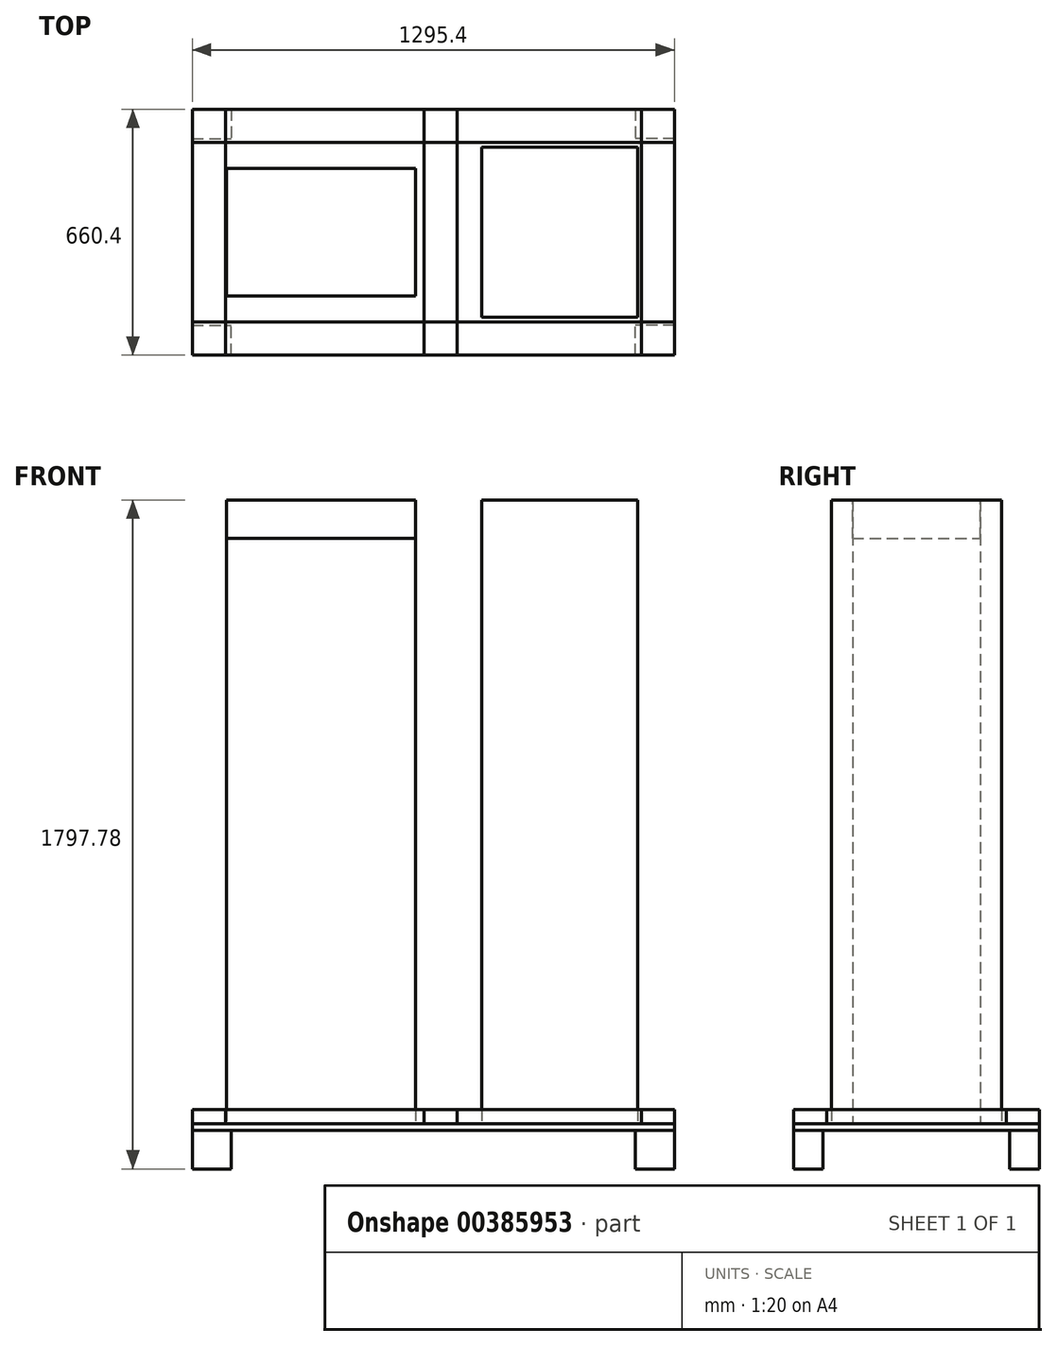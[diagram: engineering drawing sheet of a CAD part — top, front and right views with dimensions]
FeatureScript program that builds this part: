
annotation { "Feature Type Name" : "Feature", "Feature Type Description" : "" }
export const myFeature = defineFeature(function(context is Context, id is Id, definition is map)
    precondition{}
    {
        {
            var Q0;
            Q0=qCreatedBy(makeId("Top.planeOp"),FACE);
            var sketch = newSketch(context, id + "F0", { "sketchPlane" : qUnion([Q0])});
            skPoint(sketch, "E0.middle", {"position": v(0, 0) * mm});
            skLineSegment(sketch, "E1.bottom", {"start": v(647.7, -330.2) * mm, "end": v(-647.7, -330.2) * mm, "construction": true});
            skLineSegment(sketch, "E1.top", {"start": v(647.7, 330.2) * mm, "end": v(-647.7, 330.2) * mm, "construction": true});
            skLineSegment(sketch, "E1.left", {"start": v(647.7, -330.2) * mm, "end": v(647.7, 330.2) * mm, "construction": true});
            skLineSegment(sketch, "E1.right", {"start": v(-647.7, -330.2) * mm, "end": v(-647.7, 330.2) * mm, "construction": true});
            skLineSegment(sketch, "E2.bottom", {"start": v(-47.28, -171.45) * mm, "end": v(-555.28, -171.45) * mm, "construction": true});
            skLineSegment(sketch, "E2.top", {"start": v(-47.28, 171.45) * mm, "end": v(-555.28, 171.45) * mm, "construction": true});
            skLineSegment(sketch, "E2.left", {"start": v(-47.28, -171.45) * mm, "end": v(-47.28, 171.45) * mm, "construction": true});
            skLineSegment(sketch, "E2.right", {"start": v(-555.28, -171.45) * mm, "end": v(-555.28, 171.45) * mm, "construction": true});
            skPoint(sketch, "E2.middle", {"position": v(-301.28, 0) * mm});
            skLineSegment(sketch, "E3.bottom", {"start": v(549.62, 228.6) * mm, "end": v(130.52, 228.6) * mm, "construction": true});
            skLineSegment(sketch, "E3.top", {"start": v(549.62, -228.6) * mm, "end": v(130.52, -228.6) * mm, "construction": true});
            skLineSegment(sketch, "E3.left", {"start": v(549.62, 228.6) * mm, "end": v(549.62, -228.6) * mm, "construction": true});
            skLineSegment(sketch, "E3.right", {"start": v(130.52, 228.6) * mm, "end": v(130.52, -228.6) * mm, "construction": true});
            skPoint(sketch, "E3.middle", {"position": v(340.07, 0) * mm});
            skLineSegment(sketch, "E4", {"start": v(-555.28, 0) * mm, "end": v(549.62, 0) * mm, "construction": true});
            skCircle(sketch, "E5", {"center": v(-501.3, 115.89) * mm, "radius": 6.35 * mm, "construction": true});
            skCircle(sketch, "E6", {"center": v(-101.26, 115.89) * mm, "radius": 6.35 * mm, "construction": true});
            skCircle(sketch, "E7.MirrorC", {"center": v(-501.3, -115.89) * mm, "radius": 6.35 * mm, "construction": true});
            skCircle(sketch, "E8.MirrorC", {"center": v(-101.26, -115.89) * mm, "radius": 6.35 * mm, "construction": true});
            skCircle(sketch, "E9", {"center": v(155.92, 203.2) * mm, "radius": 3.18 * mm});
            skCircle(sketch, "E10", {"center": v(511.52, 203.2) * mm, "radius": 3.18 * mm});
            skCircle(sketch, "E11.MirrorC", {"center": v(155.92, -203.2) * mm, "radius": 3.18 * mm});
            skCircle(sketch, "E12.MirrorC", {"center": v(511.52, -203.2) * mm, "radius": 3.18 * mm});
            skSolve(sketch);
        }
        {
            var Q0;
            Q0=qCreatedBy(makeId("Top.planeOp"),FACE);
            var sketch = newSketch(context, id + "F1", { "sketchPlane" : qUnion([Q0])});
            skLineSegment(sketch, "E13.0", {"start": v(-47.28, 171.45) * mm, "end": v(-555.28, 171.45) * mm});
            skLineSegment(sketch, "E14.0", {"start": v(-555.28, -171.45) * mm, "end": v(-555.28, 171.45) * mm});
            skLineSegment(sketch, "E15.0", {"start": v(-47.28, -171.45) * mm, "end": v(-555.28, -171.45) * mm});
            skLineSegment(sketch, "E16.0", {"start": v(-47.28, -171.45) * mm, "end": v(-47.28, 171.45) * mm});
            skSolve(sketch);
        }
        {
            var Q0;
            Q0 = qSketchRegion(id + "F1", true);
            extrude(context, id + "F2", {"entities" : qUnion([Q0]), "depth" : 1676.4 * mm});
        }
        {
            var Q0;
            Q0=qCreatedBy(makeId("Top.planeOp"),FACE);
            var sketch = newSketch(context, id + "F3", { "sketchPlane" : qUnion([Q0])});
            skLineSegment(sketch, "E17.0", {"start": v(549.62, 228.6) * mm, "end": v(130.52, 228.6) * mm});
            skLineSegment(sketch, "E18.0", {"start": v(130.52, 228.6) * mm, "end": v(130.52, -228.6) * mm});
            skLineSegment(sketch, "E19.0", {"start": v(549.62, -228.6) * mm, "end": v(130.52, -228.6) * mm});
            skLineSegment(sketch, "E20.0", {"start": v(549.62, 228.6) * mm, "end": v(549.62, -228.6) * mm});
            skSolve(sketch);
        }
        {
            var Q0;
            Q0 = qSketchRegion(id + "F3", true);
            extrude(context, id + "F4", {"entities" : qUnion([Q0]), "depth" : 1676.4 * mm});
        }
        {
            var Q0;
            Q0=qCreatedBy(makeId("Top.planeOp"),FACE);
            cPlane(context, id + "F5", {"entities" : qUnion([Q0]), "cplaneType" : CPlaneType.OFFSET, "offset" : 18.26 * mm, "oppositeDirection" : true, "width" : 152.4 * mm, "height" : 152.4 * mm});
        }
        {
            var Q0;
            Q0=qCreatedBy(id+"F5.planeOp",FACE);
            var sketch = newSketch(context, id + "F6", { "sketchPlane" : qUnion([Q0])});
            skLineSegment(sketch, "E21.bottom", {"start": v(-647.7, -330.2) * mm, "end": v(-542.93, -330.2) * mm});
            skLineSegment(sketch, "E21.top", {"start": v(-647.7, -250.83) * mm, "end": v(-542.93, -250.83) * mm});
            skLineSegment(sketch, "E21.left", {"start": v(-647.7, -330.2) * mm, "end": v(-647.7, -250.83) * mm});
            skLineSegment(sketch, "E21.right", {"start": v(-542.93, -330.2) * mm, "end": v(-542.93, -250.83) * mm});
            skLineSegment(sketch, "E22.MirrorCS", {"start": v(647.7, -250.83) * mm, "end": v(542.93, -250.83) * mm});
            skLineSegment(sketch, "E23.MirrorCS", {"start": v(647.7, -330.2) * mm, "end": v(647.7, -250.83) * mm});
            skLineSegment(sketch, "E24.MirrorCS", {"start": v(647.7, -330.2) * mm, "end": v(542.93, -330.2) * mm});
            skLineSegment(sketch, "E25.MirrorCS", {"start": v(542.93, -330.2) * mm, "end": v(542.93, -250.83) * mm});
            skLineSegment(sketch, "E26.MirrorCS", {"start": v(-647.7, 330.2) * mm, "end": v(-647.7, 250.83) * mm});
            skLineSegment(sketch, "E27.MirrorCS", {"start": v(-542.93, 330.2) * mm, "end": v(-542.93, 250.83) * mm});
            skLineSegment(sketch, "E28.MirrorCS", {"start": v(-647.7, 330.2) * mm, "end": v(-542.93, 330.2) * mm});
            skLineSegment(sketch, "E29.MirrorCS", {"start": v(-647.7, 250.83) * mm, "end": v(-542.93, 250.83) * mm});
            skLineSegment(sketch, "E30.MirrorCS", {"start": v(647.7, 250.83) * mm, "end": v(542.93, 250.83) * mm});
            skLineSegment(sketch, "E31.MirrorCS", {"start": v(542.93, 330.2) * mm, "end": v(542.93, 250.83) * mm});
            skLineSegment(sketch, "E32.MirrorCS", {"start": v(647.7, 330.2) * mm, "end": v(542.93, 330.2) * mm});
            skLineSegment(sketch, "E33.MirrorCS", {"start": v(647.7, 330.2) * mm, "end": v(647.7, 250.83) * mm});
            skSolve(sketch);
        }
        {
            var Q0;
            Q0 = qSketchRegion(id + "F6", true);
            var Q1;
            Q1=makeQuery(id+"F2.opExtrude","CAP_FACE",FACE,{"disambiguationData":[OSD([sQuery(id+"F1.wireOp",EDGE,"E13.0"),sQuery(id+"F1.wireOp",EDGE,"E14.0"),sQuery(id+"F1.wireOp",EDGE,"E15.0"),sQuery(id+"F1.wireOp",EDGE,"E16.0")])],"isStart":false});
            extrude(context, id + "F7", {"entities" : qUnion([Q0, Q1]), "oppositeDirection" : true, "depth" : 103.12 * mm});
        }
        {
            var Q0;
            Q0=qCreatedBy(makeId("Top.planeOp"),FACE);
            var sketch = newSketch(context, id + "F8", { "sketchPlane" : qUnion([Q0])});
            skLineSegment(sketch, "E34.0", {"start": v(647.7, 330.2) * mm, "end": v(-647.7, 330.2) * mm});
            skLineSegment(sketch, "E35.0", {"start": v(-647.7, -330.2) * mm, "end": v(-647.7, 330.2) * mm});
            skLineSegment(sketch, "E36.0", {"start": v(647.7, -330.2) * mm, "end": v(-647.7, -330.2) * mm});
            skLineSegment(sketch, "E37.0", {"start": v(647.7, -330.2) * mm, "end": v(647.7, 330.2) * mm});
            skSolve(sketch);
        }
        {
            var Q0;
            Q0 = qSketchRegion(id + "F8", true);
            extrude(context, id + "F9", {"entities" : qUnion([Q0]), "oppositeDirection" : true, "depth" : 18.26 * mm});
        }
        {
            var Q0;
            Q0=makeQuery(id+"F9.opExtrude","SWEPT_FACE",FACE,{"disambiguationData":[OSD([sQuery(id+"F8.wireOp",EDGE,"E35.0")])]});
            var sketch = newSketch(context, id + "F10", { "sketchPlane" : qUnion([Q0])});
            skLineSegment(sketch, "E38.bottom", {"start": v(330.2, 0) * mm, "end": v(241.3, 0) * mm});
            skLineSegment(sketch, "E38.top", {"start": v(330.2, 38.1) * mm, "end": v(241.3, 38.1) * mm});
            skLineSegment(sketch, "E38.left", {"start": v(330.2, 0) * mm, "end": v(330.2, 38.1) * mm});
            skLineSegment(sketch, "E38.right", {"start": v(241.3, 0) * mm, "end": v(241.3, 38.1) * mm});
            skSolve(sketch);
        }
        {
            var Q0;
            Q0 = qSketchRegion(id + "F10", true);
            var Q1;
            Q1=makeQuery(id+"F9.opExtrude","SWEPT_FACE",FACE,{"disambiguationData":[OSD([sQuery(id+"F8.wireOp",EDGE,"E37.0")])]});
            extrude(context, id + "F11", {"entities" : qUnion([Q0]), "endBound" : BoundingType.UP_TO_SURFACE, "oppositeDirection" : true, "endBoundEntityFace" : qUnion([Q1]), "depth" : 25.4 * mm});
        }
        {
            var Q0;
            Q0=makeQuery(id+"F11.opExtrude","SWEPT_BODY",BODY,{"disambiguationData":[OSD([sQuery(id+"F10.wireOp",EDGE,"E38.bottom"),sQuery(id+"F10.wireOp",EDGE,"E38.top"),sQuery(id+"F10.wireOp",EDGE,"E38.left"),sQuery(id+"F10.wireOp",EDGE,"E38.right")])]});
            var Q1;
            Q1=qCreatedBy(makeId("Front.planeOp"),FACE);
            mirror(context, id + "F12", {"entities" : qUnion([Q0]), "mirrorPlane" : qUnion([Q1])});
        }
        {
            var Q0;
            Q0=makeQuery(id+"F9.opExtrude","SWEPT_FACE",FACE,{"disambiguationData":[OSD([sQuery(id+"F8.wireOp",EDGE,"E36.0")])]});
            var sketch = newSketch(context, id + "F13", { "sketchPlane" : qUnion([Q0])});
            skLineSegment(sketch, "E39.bottom", {"start": v(-647.7, 0) * mm, "end": v(-558.8, 0) * mm});
            skLineSegment(sketch, "E39.top", {"start": v(-647.7, 38.1) * mm, "end": v(-558.8, 38.1) * mm});
            skLineSegment(sketch, "E39.left", {"start": v(-647.7, 0) * mm, "end": v(-647.7, 38.1) * mm});
            skLineSegment(sketch, "E39.right", {"start": v(-558.8, 0) * mm, "end": v(-558.8, 38.1) * mm});
            skSolve(sketch);
        }
        {
            var Q0;
            Q0 = qSketchRegion(id + "F13", true);
            var Q1;
            Q1=makeQuery(id+"F12.opPattern","COPY",FACE,{"derivedFrom":makeQuery(id+"F11.opExtrude","SWEPT_FACE",FACE,{"disambiguationData":[OSD([sQuery(id+"F10.wireOp",EDGE,"E38.left")])]}),"instanceName":"1"});
            extrude(context, id + "F14", {"entities" : qUnion([Q0]), "endBound" : BoundingType.UP_TO_SURFACE, "oppositeDirection" : true, "endBoundEntityFace" : qUnion([Q1]), "depth" : 25.4 * mm});
        }
        {
            var Q0;
            Q0=makeQuery(id+"F11.opExtrude","SWEPT_EDGE",EDGE,{"disambiguationData":[OSD([sQuery(id+"F10.wireOp",EDGE,"E38.top"),sQuery(id+"F10.wireOp",EDGE,"E38.left")])]});
            cPoint(context, id + "F15", {"entities" : qUnion([Q0]), "parameter" : 0.5});
        }
        {
            var Q0;
            Q0 = qCreatedBy(id + "F15" ,VERTEX);
            var Q1;
            Q1=makeQuery(id+"F11.opExtrude","CAP_FACE",FACE,{"disambiguationData":[OSD([sQuery(id+"F10.wireOp",EDGE,"E38.bottom"),sQuery(id+"F10.wireOp",EDGE,"E38.top"),sQuery(id+"F10.wireOp",EDGE,"E38.left"),sQuery(id+"F10.wireOp",EDGE,"E38.right")])],"isStart":true});
            cPlane(context, id + "F16", {"entities" : qUnion([Q0, Q1]), "cplaneType" : CPlaneType.PLANE_POINT, "offset" : 25.4 * mm, "width" : 152.4 * mm, "height" : 152.4 * mm});
        }
        {
            var Q0;
            Q0=makeQuery(id+"F14.opExtrude","SWEPT_BODY",BODY,{"disambiguationData":[OSD([sQuery(id+"F13.wireOp",EDGE,"E39.bottom"),sQuery(id+"F13.wireOp",EDGE,"E39.top"),sQuery(id+"F13.wireOp",EDGE,"E39.left"),sQuery(id+"F13.wireOp",EDGE,"E39.right")])]});
            var Q1;
            Q1=qCreatedBy(id+"F16.planeOp",FACE);
            mirror(context, id + "F17", {"entities" : qUnion([Q0]), "mirrorPlane" : qUnion([Q1])});
        }
        {
            var Q0;
            Q0=makeQuery(id+"F11.opExtrude","CAP_FACE",FACE,{"disambiguationData":[OSD([sQuery(id+"F10.wireOp",EDGE,"E38.bottom"),sQuery(id+"F10.wireOp",EDGE,"E38.top"),sQuery(id+"F10.wireOp",EDGE,"E38.left"),sQuery(id+"F10.wireOp",EDGE,"E38.right")])],"isStart":true});
            cPlane(context, id + "F18", {"entities" : qUnion([Q0]), "cplaneType" : CPlaneType.OFFSET, "offset" : 355.6 * mm, "oppositeDirection" : true, "width" : 152.4 * mm, "height" : 152.4 * mm});
        }
        {
            var Q0;
            Q0=makeQuery(id+"F14.opExtrude","SWEPT_BODY",BODY,{"disambiguationData":[OSD([sQuery(id+"F13.wireOp",EDGE,"E39.bottom"),sQuery(id+"F13.wireOp",EDGE,"E39.top"),sQuery(id+"F13.wireOp",EDGE,"E39.left"),sQuery(id+"F13.wireOp",EDGE,"E39.right")])]});
            var Q1;
            Q1=qCreatedBy(id+"F18.planeOp",FACE);
            mirror(context, id + "F19", {"entities" : qUnion([Q0]), "mirrorPlane" : qUnion([Q1])});
        }
    });
